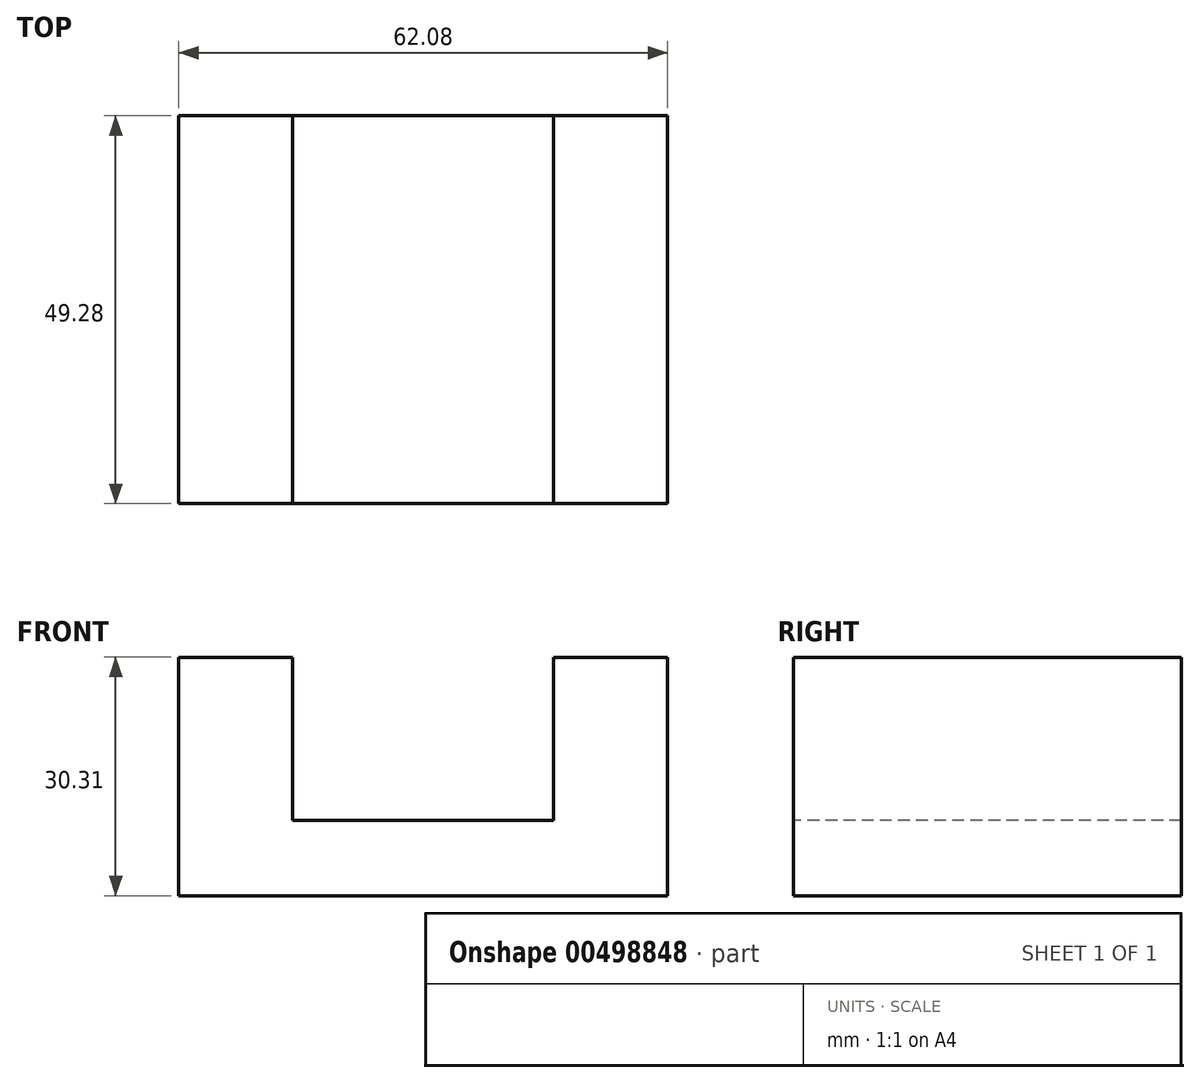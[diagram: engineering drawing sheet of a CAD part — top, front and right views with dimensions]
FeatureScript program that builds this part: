
annotation { "Feature Type Name" : "Feature", "Feature Type Description" : "" }
export const myFeature = defineFeature(function(context is Context, id is Id, definition is map)
    precondition{}
    {
        {
            var Q0;
            Q0=qCreatedBy(makeId("Front.planeOp"),FACE);
            var sketch = newSketch(context, id + "F0", { "sketchPlane" : qUnion([Q0])});
            skLineSegment(sketch, "E0.bottom", {"start": v(0, 0) * mm, "end": v(62.08, 0) * mm});
            skLineSegment(sketch, "E0.top", {"start": v(0, 30.3) * mm, "end": v(14.47, 30.3) * mm});
            skLineSegment(sketch, "E0.left", {"start": v(0, 0) * mm, "end": v(0, 30.3) * mm});
            skLineSegment(sketch, "E0.right", {"start": v(62.08, 0) * mm, "end": v(62.08, 30.3) * mm});
            skLineSegment(sketch, "E1.top", {"start": v(14.47, 9.54) * mm, "end": v(47.6, 9.54) * mm});
            skLineSegment(sketch, "E1.left", {"start": v(14.47, 30.3) * mm, "end": v(14.47, 9.54) * mm});
            skLineSegment(sketch, "E1.right", {"start": v(47.6, 30.3) * mm, "end": v(47.6, 9.54) * mm});
            skLineSegment(sketch, "E2.trimOffspring", {"start": v(47.6, 30.3) * mm, "end": v(62.08, 30.3) * mm});
            skSolve(sketch);
        }
        {
            var Q0;
            Q0=makeQuery(id+"F0.imprint","IMPRINT",FACE,{"disambiguationData":[TD([[makeQuery(id+"F0.imprint","IMPRINT",EDGE,{"derivedFrom":sQuery(id+"F0.wireOp",EDGE,"E0.bottom")}),1.0]])]});
            extrude(context, id + "F1", {"entities" : qUnion([Q0]), "oppositeDirection" : true, "depth" : 49.28 * mm, "offsetDistance" : 25.4 * mm});
        }
    });
